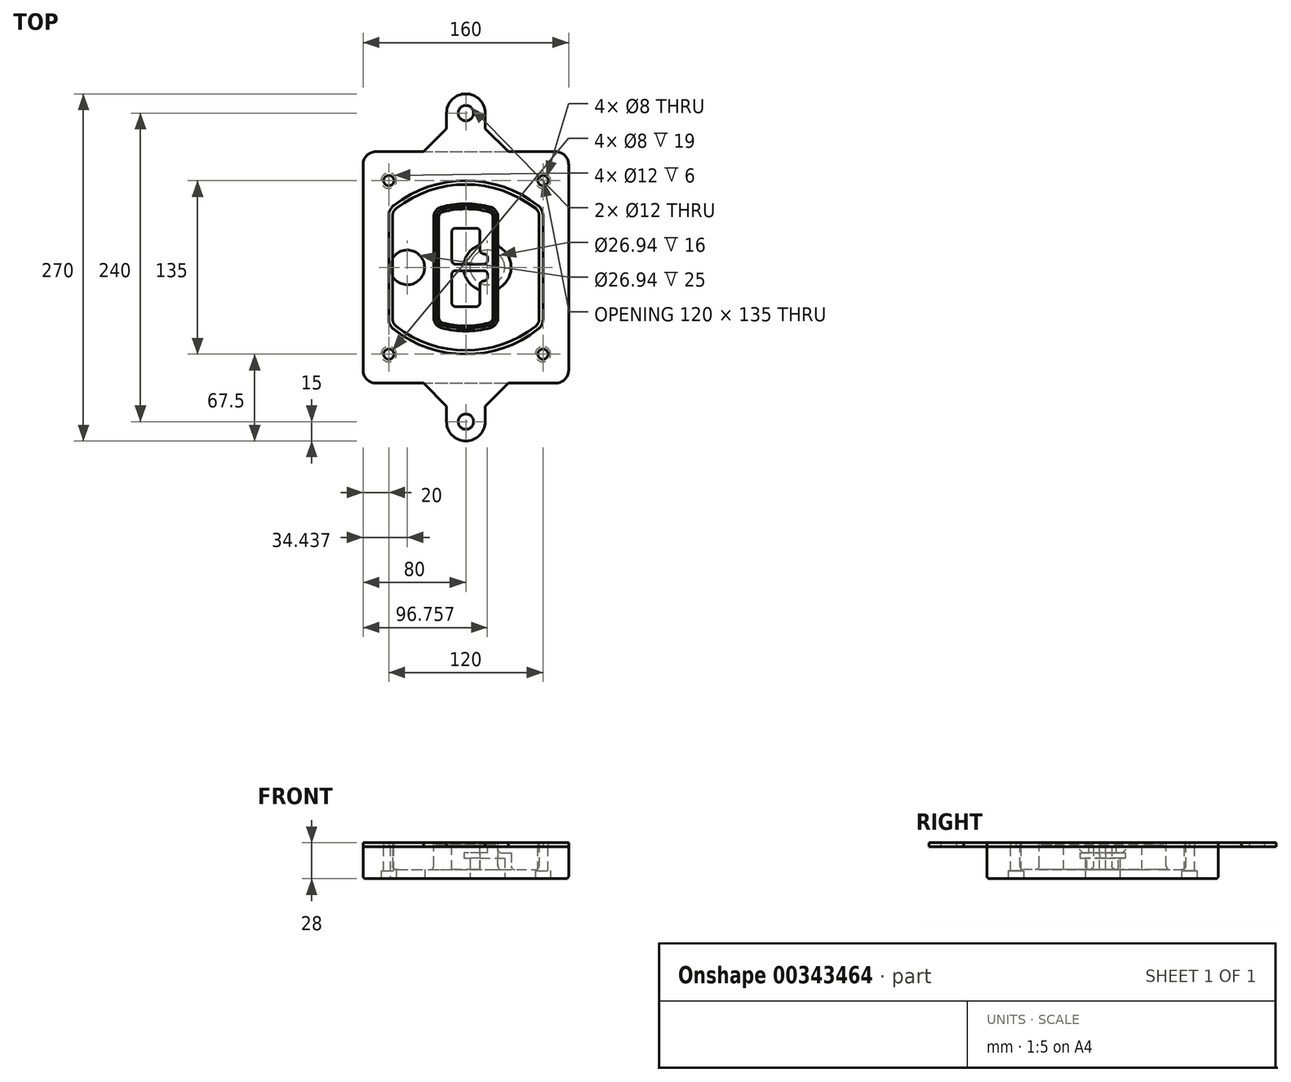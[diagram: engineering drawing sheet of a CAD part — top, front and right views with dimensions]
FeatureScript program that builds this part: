
annotation { "Feature Type Name" : "Feature", "Feature Type Description" : "" }
export const myFeature = defineFeature(function(context is Context, id is Id, definition is map)
    precondition{}
    {
        {
            var Q0;
            Q0=qCreatedBy(makeId("Top.planeOp"),FACE);
            var sketch = newSketch(context, id + "F0", { "sketchPlane" : qUnion([Q0])});
            skPoint(sketch, "E0.rect.middle", {"position": v(0, 0) * mm});
            skLineSegment(sketch, "E1.bottom", {"start": v(-70, -90) * mm, "end": v(70, -90) * mm});
            skLineSegment(sketch, "E1.top", {"start": v(-70, 90) * mm, "end": v(70, 90) * mm});
            skLineSegment(sketch, "E1.left", {"start": v(-80, -80) * mm, "end": v(-80, 80) * mm});
            skLineSegment(sketch, "E1.right", {"start": v(80, -80) * mm, "end": v(80, 80) * mm});
            skLineSegment(sketch, "E2", {"start": v(-80, 90) * mm, "end": v(80, -90) * mm, "construction": true});
            skLineSegment(sketch, "E3", {"start": v(80, 90) * mm, "end": v(-80, -90) * mm, "construction": true});
            skCircle(sketch, "E4", {"center": v(-60, 67.5) * mm, "radius": 4 * mm});
            skCircle(sketch, "E5", {"center": v(60, 67.5) * mm, "radius": 4 * mm});
            skCircle(sketch, "E6", {"center": v(60, -67.5) * mm, "radius": 4 * mm});
            skCircle(sketch, "E7", {"center": v(-60, -67.5) * mm, "radius": 4 * mm});
            skLineSegment(sketch, "E8", {"start": v(-60, 67.5) * mm, "end": v(60, 67.5) * mm, "construction": true});
            skLineSegment(sketch, "E9", {"start": v(60, 67.5) * mm, "end": v(60, -67.5) * mm, "construction": true});
            skLineSegment(sketch, "E10", {"start": v(60, -67.5) * mm, "end": v(-60, -67.5) * mm, "construction": true});
            skLineSegment(sketch, "E11", {"start": v(-60, -67.5) * mm, "end": v(-60, 67.5) * mm, "construction": true});
            skLineSegment(sketch, "E12", {"start": v(-60, 40.3) * mm, "end": v(-60, -40.3) * mm});
            skLineSegment(sketch, "E13", {"start": v(60, 40.3) * mm, "end": v(60, -40.3) * mm});
            skArc(sketch, "E14", {"start": v(56.15, 48.18) * mm, "mid": v(0, 67.5) * mm, "end": v(-56.15, 48.18) * mm});
            skArc(sketch, "E15", {"start": v(-56.15, -48.18) * mm, "mid": v(0, -67.5) * mm, "end": v(56.15, -48.18) * mm});
            skLineSegment(sketch, "E16", {"start": v(-60, 0) * mm, "end": v(60, 0) * mm, "construction": true});
            skPoint(sketch, "E17.visualSharp", {"position": v(-60, -45) * mm});
            skArc(sketch, "E17.filletArc", {"start": v(-60, -40.3) * mm, "mid": v(-58.99, -44.68) * mm, "end": v(-56.15, -48.18) * mm});
            skPoint(sketch, "E18.visualSharp", {"position": v(-60, 45) * mm});
            skArc(sketch, "E18.filletArc", {"start": v(-56.15, 48.18) * mm, "mid": v(-58.99, 44.68) * mm, "end": v(-60, 40.3) * mm});
            skPoint(sketch, "E19.visualSharp", {"position": v(60, 45) * mm});
            skArc(sketch, "E19.filletArc", {"start": v(60, 40.3) * mm, "mid": v(58.99, 44.68) * mm, "end": v(56.15, 48.18) * mm});
            skPoint(sketch, "E20.visualSharp", {"position": v(60, -45) * mm});
            skArc(sketch, "E20.filletArc", {"start": v(56.15, -48.18) * mm, "mid": v(58.99, -44.68) * mm, "end": v(60, -40.3) * mm});
            skPoint(sketch, "E21.visualSharp", {"position": v(-80, 90) * mm});
            skArc(sketch, "E21.filletArc", {"start": v(-70, 90) * mm, "mid": v(-77.07, 87.07) * mm, "end": v(-80, 80) * mm});
            skPoint(sketch, "E22.visualSharp", {"position": v(80, 90) * mm});
            skArc(sketch, "E22.filletArc", {"start": v(80, 80) * mm, "mid": v(77.07, 87.07) * mm, "end": v(70, 90) * mm});
            skPoint(sketch, "E23.visualSharp", {"position": v(80, -90) * mm});
            skArc(sketch, "E23.filletArc", {"start": v(70, -90) * mm, "mid": v(77.07, -87.07) * mm, "end": v(80, -80) * mm});
            skPoint(sketch, "E24.visualSharp", {"position": v(-80, -90) * mm});
            skArc(sketch, "E24.filletArc", {"start": v(-80, -80) * mm, "mid": v(-77.07, -87.07) * mm, "end": v(-70, -90) * mm});
            skArc(sketch, "E25.0", {"start": v(57, 40.3) * mm, "mid": v(56.3, 43.36) * mm, "end": v(54.3, 45.81) * mm});
            skLineSegment(sketch, "E25.1", {"start": v(57, 40.3) * mm, "end": v(57, -40.3) * mm});
            skArc(sketch, "E25.2", {"start": v(54.3, -45.81) * mm, "mid": v(56.3, -43.36) * mm, "end": v(57, -40.3) * mm});
            skArc(sketch, "E25.3", {"start": v(-54.3, -45.81) * mm, "mid": v(0, -64.5) * mm, "end": v(54.3, -45.81) * mm});
            skArc(sketch, "E25.4", {"start": v(-57, -40.3) * mm, "mid": v(-56.3, -43.36) * mm, "end": v(-54.3, -45.81) * mm});
            skArc(sketch, "E25.5", {"start": v(54.3, 45.81) * mm, "mid": v(0, 64.5) * mm, "end": v(-54.3, 45.81) * mm});
            skLineSegment(sketch, "E25.6", {"start": v(-57, 40.3) * mm, "end": v(-57, -40.3) * mm});
            skArc(sketch, "E25.7", {"start": v(-54.3, 45.81) * mm, "mid": v(-56.3, 43.36) * mm, "end": v(-57, 40.3) * mm});
            skArc(sketch, "E26.0", {"start": v(-58.62, 51.33) * mm, "mid": v(-62.58, 46.43) * mm, "end": v(-64, 40.3) * mm});
            skArc(sketch, "E26.1", {"start": v(58.62, 51.33) * mm, "mid": v(0, 71.5) * mm, "end": v(-58.62, 51.33) * mm});
            skArc(sketch, "E26.2", {"start": v(64, 40.3) * mm, "mid": v(62.58, 46.43) * mm, "end": v(58.62, 51.33) * mm});
            skLineSegment(sketch, "E26.3", {"start": v(64, 40.3) * mm, "end": v(64, -40.3) * mm});
            skArc(sketch, "E26.4", {"start": v(58.62, -51.33) * mm, "mid": v(62.58, -46.43) * mm, "end": v(64, -40.3) * mm});
            skLineSegment(sketch, "E26.5", {"start": v(-64, 40.3) * mm, "end": v(-64, -40.3) * mm});
            skArc(sketch, "E26.6", {"start": v(-58.62, -51.33) * mm, "mid": v(0, -71.5) * mm, "end": v(58.62, -51.33) * mm});
            skArc(sketch, "E26.7", {"start": v(-64, -40.3) * mm, "mid": v(-62.58, -46.43) * mm, "end": v(-58.62, -51.33) * mm});
            skSolve(sketch);
        }
        {
            var Q0;
            Q0=makeQuery(id+"F0.imprint","IMPRINT",FACE,{"disambiguationData":[TD([[makeQuery(id+"F0.imprint","IMPRINT",EDGE,{"derivedFrom":sQuery(id+"F0.wireOp",EDGE,"E1.bottom")}),1.0]])]});
            var Q1;
            Q1=makeQuery(id+"F0.imprint","IMPRINT",FACE,{"disambiguationData":[TD([[makeQuery(id+"F0.imprint","IMPRINT",EDGE,{"derivedFrom":sQuery(id+"F0.wireOp",EDGE,"E12")}),1.0]])]});
            var Q2;
            Q2=makeQuery(id+"F0.imprint","IMPRINT",FACE,{"disambiguationData":[TD([[makeQuery(id+"F0.imprint","IMPRINT",EDGE,{"derivedFrom":sQuery(id+"F0.wireOp",EDGE,"E25.0")}),1.0]])]});
            var Q3;
            Q3=makeQuery(id+"F0.imprint","IMPRINT",FACE,{"disambiguationData":[TD([[makeQuery(id+"F0.imprint","IMPRINT",EDGE,{"derivedFrom":sQuery(id+"F0.wireOp",EDGE,"E12")}),-1.0]])]});
            extrude(context, id + "F1", {"entities" : qUnion([Q0, Q1, Q2, Q3]), "oppositeDirection" : true, "depth" : 25 * mm});
        }
        {
            var Q0;
            Q0=makeQuery(id+"F0.imprint","IMPRINT",FACE,{"disambiguationData":[TD([[makeQuery(id+"F0.imprint","IMPRINT",EDGE,{"derivedFrom":sQuery(id+"F0.wireOp",EDGE,"E12")}),1.0]])]});
            extrude(context, id + "F2", {"entities" : qUnion([Q0]), "operationType" : NewBodyOperationType.ADD, "depth" : 3 * mm});
        }
        {
            var Q0;
            Q0=makeQuery(id+"F0.imprint","IMPRINT",FACE,{"disambiguationData":[TD([[makeQuery(id+"F0.imprint","IMPRINT",EDGE,{"derivedFrom":sQuery(id+"F0.wireOp",EDGE,"E25.0")}),1.0]])]});
            extrude(context, id + "F3", {"entities" : qUnion([Q0]), "operationType" : NewBodyOperationType.REMOVE, "oppositeDirection" : true, "depth" : 18 * mm});
        }
        {
            var Q0;
            Q0=makeQuery(id+"F2.opExtrude","CAP_FACE",FACE,{"disambiguationData":[OSD([sQuery(id+"F0.wireOp",EDGE,"E12"),sQuery(id+"F0.wireOp",EDGE,"E13"),sQuery(id+"F0.wireOp",EDGE,"E14"),sQuery(id+"F0.wireOp",EDGE,"E15"),sQuery(id+"F0.wireOp",EDGE,"E17.filletArc"),sQuery(id+"F0.wireOp",EDGE,"E18.filletArc"),sQuery(id+"F0.wireOp",EDGE,"E19.filletArc"),sQuery(id+"F0.wireOp",EDGE,"E20.filletArc"),sQuery(id+"F0.wireOp",EDGE,"E25.0"),sQuery(id+"F0.wireOp",EDGE,"E25.1"),sQuery(id+"F0.wireOp",EDGE,"E25.2"),sQuery(id+"F0.wireOp",EDGE,"E25.3"),sQuery(id+"F0.wireOp",EDGE,"E25.4"),sQuery(id+"F0.wireOp",EDGE,"E25.5"),sQuery(id+"F0.wireOp",EDGE,"E25.6"),sQuery(id+"F0.wireOp",EDGE,"E25.7")])],"isStart":false});
            var sketch = newSketch(context, id + "F4", { "sketchPlane" : qUnion([Q0])});
            skArc(sketch, "E27.0", {"start": v(-19.08, -46.97) * mm, "mid": v(0, -49.5) * mm, "end": v(19.08, -46.97) * mm});
            skArc(sketch, "E28.0", {"start": v(19.08, 46.97) * mm, "mid": v(0, 49.5) * mm, "end": v(-19.08, 46.97) * mm});
            skLineSegment(sketch, "E29", {"start": v(-25, 39.25) * mm, "end": v(-25, -39.25) * mm});
            skLineSegment(sketch, "E30", {"start": v(25, 39.25) * mm, "end": v(25, -39.25) * mm});
            skLineSegment(sketch, "E31", {"start": v(-25, 45.1) * mm, "end": v(25, 45.1) * mm, "construction": true});
            skLineSegment(sketch, "E32", {"start": v(-25, -45.1) * mm, "end": v(25, -45.1) * mm, "construction": true});
            skPoint(sketch, "E33.visualSharp", {"position": v(-25, 45.1) * mm});
            skArc(sketch, "E33.filletArc", {"start": v(-19.08, 46.97) * mm, "mid": v(-23.35, 44.11) * mm, "end": v(-25, 39.25) * mm});
            skPoint(sketch, "E34.visualSharp", {"position": v(25, 45.1) * mm});
            skArc(sketch, "E34.filletArc", {"start": v(25, 39.25) * mm, "mid": v(23.35, 44.11) * mm, "end": v(19.08, 46.97) * mm});
            skPoint(sketch, "E35.visualSharp", {"position": v(25, -45.1) * mm});
            skArc(sketch, "E35.filletArc", {"start": v(19.08, -46.97) * mm, "mid": v(23.35, -44.11) * mm, "end": v(25, -39.25) * mm});
            skPoint(sketch, "E36.visualSharp", {"position": v(-25, -45.1) * mm});
            skArc(sketch, "E36.filletArc", {"start": v(-25, -39.25) * mm, "mid": v(-23.35, -44.11) * mm, "end": v(-19.08, -46.97) * mm});
            skArc(sketch, "E37.0", {"start": v(54.3, 45.81) * mm, "mid": v(0, 64.5) * mm, "end": v(-54.3, 45.81) * mm});
            skArc(sketch, "E37.1", {"start": v(-54.3, 45.81) * mm, "mid": v(-56.3, 43.36) * mm, "end": v(-57, 40.3) * mm});
            skLineSegment(sketch, "E37.2", {"start": v(-57, 40.3) * mm, "end": v(-57, -40.3) * mm});
            skArc(sketch, "E37.3", {"start": v(-57, -40.3) * mm, "mid": v(-56.3, -43.36) * mm, "end": v(-54.3, -45.81) * mm});
            skArc(sketch, "E37.4", {"start": v(-54.3, -45.81) * mm, "mid": v(0, -64.5) * mm, "end": v(54.3, -45.81) * mm});
            skArc(sketch, "E37.5", {"start": v(54.3, -45.81) * mm, "mid": v(56.3, -43.36) * mm, "end": v(57, -40.3) * mm});
            skLineSegment(sketch, "E37.6", {"start": v(57, 40.3) * mm, "end": v(57, -40.3) * mm});
            skArc(sketch, "E37.7", {"start": v(57, 40.3) * mm, "mid": v(56.3, 43.36) * mm, "end": v(54.3, 45.81) * mm});
            skLineSegment(sketch, "E38.0", {"start": v(23, 39.25) * mm, "end": v(23, -39.25) * mm});
            skArc(sketch, "E38.1", {"start": v(18.56, -45.04) * mm, "mid": v(21.76, -42.9) * mm, "end": v(23, -39.25) * mm});
            skArc(sketch, "E38.2", {"start": v(-18.56, -45.04) * mm, "mid": v(0, -47.5) * mm, "end": v(18.56, -45.04) * mm});
            skArc(sketch, "E38.3", {"start": v(-23, -39.25) * mm, "mid": v(-21.76, -42.9) * mm, "end": v(-18.56, -45.04) * mm});
            skLineSegment(sketch, "E38.4", {"start": v(-23, 39.25) * mm, "end": v(-23, -39.25) * mm});
            skArc(sketch, "E38.5", {"start": v(23, 39.25) * mm, "mid": v(21.76, 42.9) * mm, "end": v(18.56, 45.04) * mm});
            skArc(sketch, "E38.6", {"start": v(-18.56, 45.04) * mm, "mid": v(-21.76, 42.9) * mm, "end": v(-23, 39.25) * mm});
            skArc(sketch, "E38.7", {"start": v(18.56, 45.04) * mm, "mid": v(0, 47.5) * mm, "end": v(-18.56, 45.04) * mm});
            skArc(sketch, "E39.0", {"start": v(21, 39.25) * mm, "mid": v(20.18, 41.68) * mm, "end": v(18.04, 43.1) * mm});
            skLineSegment(sketch, "E39.1", {"start": v(21, 39.25) * mm, "end": v(21, -39.25) * mm});
            skArc(sketch, "E39.2", {"start": v(18.04, -43.1) * mm, "mid": v(20.18, -41.68) * mm, "end": v(21, -39.25) * mm});
            skArc(sketch, "E39.3", {"start": v(-18.04, -43.1) * mm, "mid": v(0, -45.5) * mm, "end": v(18.04, -43.1) * mm});
            skArc(sketch, "E39.4", {"start": v(-21, -39.25) * mm, "mid": v(-20.18, -41.68) * mm, "end": v(-18.04, -43.1) * mm});
            skArc(sketch, "E39.5", {"start": v(18.04, 43.1) * mm, "mid": v(0, 45.5) * mm, "end": v(-18.04, 43.1) * mm});
            skLineSegment(sketch, "E39.6", {"start": v(-21, 39.25) * mm, "end": v(-21, -39.25) * mm});
            skArc(sketch, "E39.7", {"start": v(-18.04, 43.1) * mm, "mid": v(-20.18, 41.68) * mm, "end": v(-21, 39.25) * mm});
            skLineSegment(sketch, "E40", {"start": v(-25, 0) * mm, "end": v(25, 0) * mm, "construction": true});
            skLineSegment(sketch, "E41", {"start": v(-11, 5.5) * mm, "end": v(-11, 27.5) * mm});
            skLineSegment(sketch, "E42", {"start": v(-8, 30.5) * mm, "end": v(8, 30.5) * mm});
            skLineSegment(sketch, "E43", {"start": v(11, 27.5) * mm, "end": v(11, 13.5) * mm});
            skLineSegment(sketch, "E44", {"start": v(14, 10.5) * mm, "end": v(14, 10.5) * mm});
            skLineSegment(sketch, "E45", {"start": v(17, 7.5) * mm, "end": v(17, 5.5) * mm});
            skLineSegment(sketch, "E46", {"start": v(14, 2.5) * mm, "end": v(-8, 2.5) * mm});
            skPoint(sketch, "E47.visualSharp", {"position": v(-11, 30.5) * mm});
            skArc(sketch, "E47.filletArc", {"start": v(-8, 30.5) * mm, "mid": v(-10.12, 29.62) * mm, "end": v(-11, 27.5) * mm});
            skPoint(sketch, "E48.visualSharp", {"position": v(11, 30.5) * mm});
            skArc(sketch, "E48.filletArc", {"start": v(11, 27.5) * mm, "mid": v(10.12, 29.62) * mm, "end": v(8, 30.5) * mm});
            skPoint(sketch, "E49.visualSharp", {"position": v(11, 10.5) * mm});
            skArc(sketch, "E49.filletArc", {"start": v(11, 13.5) * mm, "mid": v(11.88, 11.38) * mm, "end": v(14, 10.5) * mm});
            skPoint(sketch, "E50.visualSharp", {"position": v(17, 10.5) * mm});
            skArc(sketch, "E50.filletArc", {"start": v(17, 7.5) * mm, "mid": v(16.12, 9.62) * mm, "end": v(14, 10.5) * mm});
            skPoint(sketch, "E51.visualSharp", {"position": v(17, 2.5) * mm});
            skArc(sketch, "E51.filletArc", {"start": v(14, 2.5) * mm, "mid": v(16.12, 3.38) * mm, "end": v(17, 5.5) * mm});
            skPoint(sketch, "E52.visualSharp", {"position": v(-11, 2.5) * mm});
            skArc(sketch, "E52.filletArc", {"start": v(-11, 5.5) * mm, "mid": v(-10.12, 3.38) * mm, "end": v(-8, 2.5) * mm});
            skLineSegment(sketch, "E53.0.MirrorCS", {"start": v(14, -2.5) * mm, "end": v(-8, -2.5) * mm});
            skArc(sketch, "E54.0.MirrorCS", {"start": v(-11, -5.5) * mm, "mid": v(-10.12, -3.38) * mm, "end": v(-8, -2.5) * mm});
            skLineSegment(sketch, "E55.0.MirrorCS", {"start": v(-11, -5.5) * mm, "end": v(-11, -27.5) * mm});
            skArc(sketch, "E56.0.MirrorCS", {"start": v(-8, -30.5) * mm, "mid": v(-10.12, -29.62) * mm, "end": v(-11, -27.5) * mm});
            skLineSegment(sketch, "E57.0.MirrorCS", {"start": v(-8, -30.5) * mm, "end": v(8, -30.5) * mm});
            skArc(sketch, "E58.0.MirrorCS", {"start": v(11, -27.5) * mm, "mid": v(10.12, -29.62) * mm, "end": v(8, -30.5) * mm});
            skLineSegment(sketch, "E59.0.MirrorCS", {"start": v(11, -27.5) * mm, "end": v(11, -13.5) * mm});
            skArc(sketch, "E60.0.MirrorCS", {"start": v(11, -13.5) * mm, "mid": v(11.88, -11.38) * mm, "end": v(14, -10.5) * mm});
            skArc(sketch, "E61.0.MirrorCS", {"start": v(17, -7.5) * mm, "mid": v(16.12, -9.62) * mm, "end": v(14, -10.5) * mm});
            skLineSegment(sketch, "E62.0.MirrorCS", {"start": v(17, -7.5) * mm, "end": v(17, -5.5) * mm});
            skArc(sketch, "E63.0.MirrorCS", {"start": v(14, -2.5) * mm, "mid": v(16.12, -3.38) * mm, "end": v(17, -5.5) * mm});
            skSolve(sketch);
        }
        {
            var Q0;
            Q0=makeQuery(id+"F4.imprint","IMPRINT",FACE,{"disambiguationData":[TD([[makeQuery(id+"F4.imprint","IMPRINT",EDGE,{"derivedFrom":sQuery(id+"F4.wireOp",EDGE,"E27.0")}),1.0]])]});
            var Q1;
            Q1=makeQuery(id+"F4.imprint","IMPRINT",FACE,{"disambiguationData":[TD([[makeQuery(id+"F4.imprint","IMPRINT",EDGE,{"derivedFrom":sQuery(id+"F4.wireOp",EDGE,"E38.0")}),-1.0]])]});
            var Q2;
            Q2=makeQuery(id+"F4.imprint","IMPRINT",FACE,{"disambiguationData":[TD([[makeQuery(id+"F4.imprint","IMPRINT",EDGE,{"derivedFrom":sQuery(id+"F4.wireOp",EDGE,"E39.0")}),1.0]])]});
            extrude(context, id + "F5", {"entities" : qUnion([Q0, Q1, Q2]), "operationType" : NewBodyOperationType.ADD, "endBound" : BoundingType.UP_TO_NEXT, "oppositeDirection" : true, "depth" : 25 * mm});
        }
        {
            var Q0;
            Q0=makeQuery(id+"F4.imprint","IMPRINT",FACE,{"disambiguationData":[TD([[makeQuery(id+"F4.imprint","IMPRINT",EDGE,{"derivedFrom":sQuery(id+"F4.wireOp",EDGE,"E38.0")}),-1.0]])]});
            extrude(context, id + "F6", {"entities" : qUnion([Q0]), "operationType" : NewBodyOperationType.REMOVE, "oppositeDirection" : true, "depth" : 2 * mm});
        }
        {
            var Q0;
            Q0=makeQuery(id+"F1.opExtrude","CAP_FACE",FACE,{"disambiguationData":[OSD([sQuery(id+"F0.wireOp",EDGE,"E1.bottom"),sQuery(id+"F0.wireOp",EDGE,"E1.top"),sQuery(id+"F0.wireOp",EDGE,"E1.left"),sQuery(id+"F0.wireOp",EDGE,"E1.right"),sQuery(id+"F0.wireOp",EDGE,"E4"),sQuery(id+"F0.wireOp",EDGE,"E5"),sQuery(id+"F0.wireOp",EDGE,"E6"),sQuery(id+"F0.wireOp",EDGE,"E7"),sQuery(id+"F0.wireOp",EDGE,"E21.filletArc"),sQuery(id+"F0.wireOp",EDGE,"E22.filletArc"),sQuery(id+"F0.wireOp",EDGE,"E23.filletArc"),sQuery(id+"F0.wireOp",EDGE,"E24.filletArc")])],"isStart":false});
            var sketch = newSketch(context, id + "F7", { "sketchPlane" : qUnion([Q0])});
            skCircle(sketch, "E64", {"center": v(16.76, 0) * mm, "radius": 13.47 * mm});
            skCircle(sketch, "E65", {"center": v(-45.56, 0) * mm, "radius": 13.47 * mm});
            skLineSegment(sketch, "E66", {"start": v(80, 0) * mm, "end": v(-80, 0) * mm});
            skCircle(sketch, "E67", {"center": v(16.76, 0) * mm, "radius": 18.47 * mm});
            skCircle(sketch, "E68", {"center": v(60, -67.5) * mm, "radius": 6 * mm});
            skCircle(sketch, "E69", {"center": v(-60, -67.5) * mm, "radius": 6 * mm});
            skCircle(sketch, "E70", {"center": v(-60, 67.5) * mm, "radius": 6 * mm});
            skCircle(sketch, "E71", {"center": v(60, 67.5) * mm, "radius": 6 * mm});
            skSolve(sketch);
        }
        {
            var Q0;
            {var subQ1=sQuery(id+"F7.wireOp",EDGE,"E66");var subQ4=sQuery(id+"F7.wireOp",EDGE,"E64");var subQ6=makeQuery(id+"F7.imprint","INTERSECT",VERTEX,{"disambiguationData":[OD(0.0)],"derivedFrom":[subQ4,subQ1]});Q0=makeQuery(id+"F7.imprint","IMPRINT",FACE,{"disambiguationData":[TD([[makeQuery(id+"F7.imprint","IMPRINT",EDGE,{"disambiguationData":[TD([[subQ6,-1.0]])],"derivedFrom":subQ4}),-1.0]])]});}
            var Q1;
            {var subQ0=sQuery(id+"F7.wireOp",EDGE,"E66");var subQ1=sQuery(id+"F7.wireOp",EDGE,"E64");var subQ3=makeQuery(id+"F7.imprint","INTERSECT",VERTEX,{"disambiguationData":[OD(0.0)],"derivedFrom":[subQ1,subQ0]});Q1=makeQuery(id+"F7.imprint","IMPRINT",FACE,{"disambiguationData":[TD([[makeQuery(id+"F7.imprint","IMPRINT",EDGE,{"disambiguationData":[TD([[subQ3,-1.0]])],"derivedFrom":subQ1}),1.0]])]});}
            var Q2;
            {var subQ0=sQuery(id+"F7.wireOp",EDGE,"E66");var subQ1=sQuery(id+"F7.wireOp",EDGE,"E64");var subQ3=makeQuery(id+"F7.imprint","INTERSECT",VERTEX,{"disambiguationData":[OD(0.0)],"derivedFrom":[subQ1,subQ0]});Q2=makeQuery(id+"F7.imprint","IMPRINT",FACE,{"disambiguationData":[TD([[makeQuery(id+"F7.imprint","IMPRINT",EDGE,{"disambiguationData":[TD([[subQ3,1.0]])],"derivedFrom":subQ1}),1.0]])]});}
            var Q3;
            {var subQ1=sQuery(id+"F7.wireOp",EDGE,"E66");var subQ4=sQuery(id+"F7.wireOp",EDGE,"E64");var subQ6=makeQuery(id+"F7.imprint","INTERSECT",VERTEX,{"disambiguationData":[OD(0.0)],"derivedFrom":[subQ4,subQ1]});Q3=makeQuery(id+"F7.imprint","IMPRINT",FACE,{"disambiguationData":[TD([[makeQuery(id+"F7.imprint","IMPRINT",EDGE,{"disambiguationData":[TD([[subQ6,1.0]])],"derivedFrom":subQ4}),-1.0]])]});}
            extrude(context, id + "F8", {"entities" : qUnion([Q0, Q1, Q2, Q3]), "operationType" : NewBodyOperationType.ADD, "oppositeDirection" : true, "depth" : 20 * mm});
        }
        {
            var Q0;
            {var subQ0=sQuery(id+"F7.wireOp",EDGE,"E66");var subQ1=sQuery(id+"F7.wireOp",EDGE,"E64");var subQ3=makeQuery(id+"F7.imprint","INTERSECT",VERTEX,{"disambiguationData":[OD(0.0)],"derivedFrom":[subQ1,subQ0]});Q0=makeQuery(id+"F7.imprint","IMPRINT",FACE,{"disambiguationData":[TD([[makeQuery(id+"F7.imprint","IMPRINT",EDGE,{"disambiguationData":[TD([[subQ3,-1.0]])],"derivedFrom":subQ1}),1.0]])]});}
            var Q1;
            {var subQ0=sQuery(id+"F7.wireOp",EDGE,"E66");var subQ1=sQuery(id+"F7.wireOp",EDGE,"E64");var subQ3=makeQuery(id+"F7.imprint","INTERSECT",VERTEX,{"disambiguationData":[OD(0.0)],"derivedFrom":[subQ1,subQ0]});Q1=makeQuery(id+"F7.imprint","IMPRINT",FACE,{"disambiguationData":[TD([[makeQuery(id+"F7.imprint","IMPRINT",EDGE,{"disambiguationData":[TD([[subQ3,1.0]])],"derivedFrom":subQ1}),1.0]])]});}
            extrude(context, id + "F9", {"entities" : qUnion([Q0, Q1]), "operationType" : NewBodyOperationType.REMOVE, "oppositeDirection" : true, "depth" : 16 * mm});
        }
        {
            var Q0;
            {var subQ0=sQuery(id+"F7.wireOp",EDGE,"E66");var subQ1=sQuery(id+"F7.wireOp",EDGE,"E65");var subQ3=makeQuery(id+"F7.imprint","INTERSECT",VERTEX,{"disambiguationData":[OD(0.0)],"derivedFrom":[subQ1,subQ0]});Q0=makeQuery(id+"F7.imprint","IMPRINT",FACE,{"disambiguationData":[TD([[makeQuery(id+"F7.imprint","IMPRINT",EDGE,{"disambiguationData":[TD([[subQ3,-1.0]])],"derivedFrom":subQ1}),1.0]])]});}
            var Q1;
            {var subQ0=sQuery(id+"F7.wireOp",EDGE,"E66");var subQ1=sQuery(id+"F7.wireOp",EDGE,"E65");var subQ3=makeQuery(id+"F7.imprint","INTERSECT",VERTEX,{"disambiguationData":[OD(0.0)],"derivedFrom":[subQ1,subQ0]});Q1=makeQuery(id+"F7.imprint","IMPRINT",FACE,{"disambiguationData":[TD([[makeQuery(id+"F7.imprint","IMPRINT",EDGE,{"disambiguationData":[TD([[subQ3,1.0]])],"derivedFrom":subQ1}),1.0]])]});}
            extrude(context, id + "F10", {"entities" : qUnion([Q0, Q1]), "operationType" : NewBodyOperationType.REMOVE, "oppositeDirection" : true, "depth" : 25 * mm});
        }
        {
            var Q0;
            Q0=makeQuery(id+"F7.imprint","IMPRINT",FACE,{"disambiguationData":[TD([[makeQuery(id+"F7.imprint","IMPRINT",EDGE,{"derivedFrom":sQuery(id+"F7.wireOp",EDGE,"E68")}),1.0]])]});
            var Q1;
            Q1=makeQuery(id+"F7.imprint","IMPRINT",FACE,{"disambiguationData":[TD([[makeQuery(id+"F7.imprint","IMPRINT",EDGE,{"derivedFrom":makeQuery(id+"F1.opExtrude","CAP_EDGE",EDGE,{"disambiguationData":[OSD([sQuery(id+"F0.wireOp",EDGE,"E5")])],"isStart":false})}),-1.0]])]});
            var Q2;
            Q2=makeQuery(id+"F7.imprint","IMPRINT",FACE,{"disambiguationData":[TD([[makeQuery(id+"F7.imprint","IMPRINT",EDGE,{"derivedFrom":sQuery(id+"F7.wireOp",EDGE,"E69")}),1.0]])]});
            var Q3;
            Q3=makeQuery(id+"F7.imprint","IMPRINT",FACE,{"disambiguationData":[TD([[makeQuery(id+"F7.imprint","IMPRINT",EDGE,{"derivedFrom":makeQuery(id+"F1.opExtrude","CAP_EDGE",EDGE,{"disambiguationData":[OSD([sQuery(id+"F0.wireOp",EDGE,"E4")])],"isStart":false})}),-1.0]])]});
            var Q4;
            Q4=makeQuery(id+"F7.imprint","IMPRINT",FACE,{"disambiguationData":[TD([[makeQuery(id+"F7.imprint","IMPRINT",EDGE,{"derivedFrom":sQuery(id+"F7.wireOp",EDGE,"E70")}),1.0]])]});
            var Q5;
            Q5=makeQuery(id+"F7.imprint","IMPRINT",FACE,{"disambiguationData":[TD([[makeQuery(id+"F7.imprint","IMPRINT",EDGE,{"derivedFrom":makeQuery(id+"F1.opExtrude","CAP_EDGE",EDGE,{"disambiguationData":[OSD([sQuery(id+"F0.wireOp",EDGE,"E7")])],"isStart":false})}),-1.0]])]});
            var Q6;
            Q6=makeQuery(id+"F7.imprint","IMPRINT",FACE,{"disambiguationData":[TD([[makeQuery(id+"F7.imprint","IMPRINT",EDGE,{"derivedFrom":sQuery(id+"F7.wireOp",EDGE,"E71")}),1.0]])]});
            var Q7;
            Q7=makeQuery(id+"F7.imprint","IMPRINT",FACE,{"disambiguationData":[TD([[makeQuery(id+"F7.imprint","IMPRINT",EDGE,{"derivedFrom":makeQuery(id+"F1.opExtrude","CAP_EDGE",EDGE,{"disambiguationData":[OSD([sQuery(id+"F0.wireOp",EDGE,"E6")])],"isStart":false})}),-1.0]])]});
            extrude(context, id + "F11", {"entities" : qUnion([Q0, Q1, Q2, Q3, Q4, Q5, Q6, Q7]), "operationType" : NewBodyOperationType.REMOVE, "oppositeDirection" : true, "depth" : 6 * mm});
        }
        {
            var Q0;
            Q0=makeQuery(id+"F9.boolean.opBoolean","COPY",FACE,{"derivedFrom":makeQuery(id+"F9.opExtrude","CAP_FACE",FACE,{"disambiguationData":[OSD([sQuery(id+"F7.wireOp",EDGE,"E64")])],"isStart":false})});
            var sketch = newSketch(context, id + "F12", { "sketchPlane" : qUnion([Q0])});
            skArc(sketch, "E72.0", {"start": v(11, 17.55) * mm, "mid": v(2.57, 11.82) * mm, "end": v(-1.54, 2.5) * mm});
            skArc(sketch, "E72.1", {"start": v(-1.54, -2.5) * mm, "mid": v(2.57, -11.82) * mm, "end": v(11, -17.55) * mm});
            skLineSegment(sketch, "E73", {"start": v(-1.54, -2.5) * mm, "end": v(14, -2.5) * mm});
            skLineSegment(sketch, "E74.0", {"start": v(14, 2.5) * mm, "end": v(-1.54, 2.5) * mm});
            skArc(sketch, "E74.1", {"start": v(14, 2.5) * mm, "mid": v(16.12, 3.38) * mm, "end": v(17, 5.5) * mm});
            skLineSegment(sketch, "E74.2", {"start": v(17, 7.5) * mm, "end": v(17, 5.5) * mm});
            skArc(sketch, "E74.3", {"start": v(17, 7.5) * mm, "mid": v(16.12, 9.62) * mm, "end": v(14, 10.5) * mm});
            skArc(sketch, "E74.4", {"start": v(11, 13.5) * mm, "mid": v(11.88, 11.38) * mm, "end": v(14, 10.5) * mm});
            skLineSegment(sketch, "E74.5", {"start": v(11, 17.55) * mm, "end": v(11, 13.5) * mm});
            skLineSegment(sketch, "E74.7", {"start": v(14, -2.5) * mm, "end": v(-1.54, -2.5) * mm});
            skArc(sketch, "E74.8", {"start": v(14, -2.5) * mm, "mid": v(16.12, -3.38) * mm, "end": v(17, -5.5) * mm});
            skLineSegment(sketch, "E74.9", {"start": v(17, -7.5) * mm, "end": v(17, -5.5) * mm});
            skArc(sketch, "E74.10", {"start": v(17, -7.5) * mm, "mid": v(16.12, -9.62) * mm, "end": v(14, -10.5) * mm});
            skArc(sketch, "E74.11", {"start": v(11, -13.5) * mm, "mid": v(11.88, -11.38) * mm, "end": v(14, -10.5) * mm});
            skLineSegment(sketch, "E74.12", {"start": v(11, -17.55) * mm, "end": v(11, -13.5) * mm});
            skPoint(sketch, "E75.orphan", {"position": v(11, -27.5) * mm});
            skPoint(sketch, "E76.orphan", {"position": v(-8, -2.5) * mm});
            skPoint(sketch, "E77.orphan", {"position": v(-8, 2.5) * mm});
            skPoint(sketch, "E78.orphan", {"position": v(11, 27.5) * mm});
            skSolve(sketch);
        }
        {
            var Q0;
            {var subQ7=sQuery(id+"F12.wireOp",EDGE,"E72.0");var subQ14=sQuery(id+"F12.wireOp",EDGE,"E72.1");var subQ16=sQuery(id+"F12.wireOp",EDGE,"E74.1");var subQ18=sQuery(id+"F12.wireOp",EDGE,"E74.8");Q0=qUnion([makeQuery(id+"F12.imprint","IMPRINT",FACE,{"disambiguationData":[TD([[makeQuery(id+"F12.imprint","IMPRINT",EDGE,{"derivedFrom":subQ7}),1.0]])]}),makeQuery(id+"F12.imprint","IMPRINT",FACE,{"disambiguationData":[TD([[makeQuery(id+"F12.imprint","IMPRINT",EDGE,{"derivedFrom":subQ14}),1.0]])]}),makeQuery(id+"F12.imprint","IMPRINT",FACE,{"disambiguationData":[TD([[makeQuery(id+"F12.imprint","IMPRINT",EDGE,{"derivedFrom":subQ16}),1.0]])]}),makeQuery(id+"F12.imprint","IMPRINT",FACE,{"disambiguationData":[TD([[makeQuery(id+"F12.imprint","IMPRINT",EDGE,{"derivedFrom":subQ18}),-1.0]])]})]);}
            var Q1;
            Q1=makeQuery(id+"F5.boolean.opBoolean","SPLIT",FACE,{"disambiguationData":[TD([makeQuery(id+"F5.opExtrude","SWEPT_FACE",FACE,{"disambiguationData":[OSD([sQuery(id+"F4.wireOp",EDGE,"E41")])]})])],"derivedFrom":makeQuery(id+"F3.boolean.opBoolean","COPY",FACE,{"derivedFrom":makeQuery(id+"F3.opExtrude","CAP_FACE",FACE,{"disambiguationData":[OSD([sQuery(id+"F0.wireOp",EDGE,"E25.0"),sQuery(id+"F0.wireOp",EDGE,"E25.1"),sQuery(id+"F0.wireOp",EDGE,"E25.2"),sQuery(id+"F0.wireOp",EDGE,"E25.3"),sQuery(id+"F0.wireOp",EDGE,"E25.4"),sQuery(id+"F0.wireOp",EDGE,"E25.5"),sQuery(id+"F0.wireOp",EDGE,"E25.6"),sQuery(id+"F0.wireOp",EDGE,"E25.7")])],"isStart":false})})});
            extrude(context, id + "F13", {"entities" : qUnion([Q0]), "operationType" : NewBodyOperationType.REMOVE, "endBound" : BoundingType.UP_TO_SURFACE, "endBoundEntityFace" : qUnion([Q1]), "depth" : 25 * mm});
        }
        {
            var Q0;
            Q0=makeQuery(id+"F3.boolean.opBoolean","COPY",EDGE,{"derivedFrom":makeQuery(id+"F3.opExtrude","CAP_EDGE",EDGE,{"disambiguationData":[OSD([sQuery(id+"F0.wireOp",EDGE,"E25.6")])],"isStart":false})});
            var Q1;
            Q1=makeQuery(id+"F8.boolean.opBoolean","INTERSECT",EDGE,{"derivedFrom":[makeQuery(id+"F5.opExtrude","SWEPT_FACE",FACE,{"disambiguationData":[OSD([sQuery(id+"F4.wireOp",EDGE,"E30")])]}),makeQuery(id+"F8.opExtrude","CAP_FACE",FACE,{"disambiguationData":[OSD([sQuery(id+"F7.wireOp",EDGE,"E67")])],"isStart":false})]});
            var Q2;
            Q2=makeQuery(id+"F8.boolean.opBoolean","INTERSECT",EDGE,{"disambiguationData":[OD(1.0)],"derivedFrom":[makeQuery(id+"F5.opExtrude","SWEPT_FACE",FACE,{"disambiguationData":[OSD([sQuery(id+"F4.wireOp",EDGE,"E30")])]}),makeQuery(id+"F8.opExtrude","SWEPT_FACE",FACE,{"disambiguationData":[OSD([sQuery(id+"F7.wireOp",EDGE,"E67")])]})]});
            var Q3;
            {var subQ0=sQuery(id+"F4.wireOp",EDGE,"E30");Q3=makeQuery(id+"F8.boolean.opBoolean","SPLIT",EDGE,{"disambiguationData":[TD([makeQuery(id+"F5.opExtrude","SWEPT_FACE",FACE,{"disambiguationData":[OSD([sQuery(id+"F4.wireOp",EDGE,"E35.filletArc")])]})])],"derivedFrom":makeQuery(id+"F5.opExtrude","CAP_EDGE",EDGE,{"disambiguationData":[OSD([subQ0])],"isStart":false})});}
            var Q4;
            {var subQ0=sQuery(id+"F0.wireOp",EDGE,"E25.7");var subQ1=sQuery(id+"F0.wireOp",EDGE,"E25.1");var subQ2=sQuery(id+"F0.wireOp",EDGE,"E25.6");var subQ3=sQuery(id+"F0.wireOp",EDGE,"E25.5");var subQ4=sQuery(id+"F0.wireOp",EDGE,"E25.4");var subQ5=sQuery(id+"F0.wireOp",EDGE,"E25.0");var subQ6=sQuery(id+"F0.wireOp",EDGE,"E25.2");var subQ7=sQuery(id+"F0.wireOp",EDGE,"E25.3");Q4=makeQuery(id+"F8.boolean.opBoolean","INTERSECT",EDGE,{"derivedFrom":[makeQuery(id+"F5.boolean.opBoolean","SPLIT",FACE,{"disambiguationData":[TD([makeQuery(id+"F2.opExtrude","SWEPT_FACE",FACE,{"disambiguationData":[OSD([subQ5])]})])],"derivedFrom":makeQuery(id+"F3.boolean.opBoolean","COPY",FACE,{"derivedFrom":makeQuery(id+"F3.opExtrude","CAP_FACE",FACE,{"disambiguationData":[OSD([subQ5,subQ1,subQ6,subQ7,subQ4,subQ3,subQ2,subQ0])],"isStart":false})})}),makeQuery(id+"F8.opExtrude","SWEPT_FACE",FACE,{"disambiguationData":[OSD([sQuery(id+"F7.wireOp",EDGE,"E67")])]})]});}
            var Q5;
            Q5=makeQuery(id+"F8.boolean.opBoolean","INTERSECT",EDGE,{"disambiguationData":[OD(0.0)],"derivedFrom":[makeQuery(id+"F5.opExtrude","SWEPT_FACE",FACE,{"disambiguationData":[OSD([sQuery(id+"F4.wireOp",EDGE,"E30")])]}),makeQuery(id+"F8.opExtrude","SWEPT_FACE",FACE,{"disambiguationData":[OSD([sQuery(id+"F7.wireOp",EDGE,"E67")])]})]});
            fillet(context, id + "F14", {"entities" : qUnion([Q0, Q1, Q2, Q3, Q4, Q5]), "radius" : 3 * mm, "tangentPropagation" : true, "allowEdgeOverflow" : false});
        }
        {
            var Q0;
            Q0=makeQuery(id+"F1.opExtrude","CAP_EDGE",EDGE,{"disambiguationData":[OSD([sQuery(id+"F0.wireOp",EDGE,"E1.bottom")])],"isStart":false});
            fillet(context, id + "F15", {"entities" : qUnion([Q0]), "radius" : 2 * mm, "tangentPropagation" : true, "allowEdgeOverflow" : false});
        }
        {
            var Q0;
            {var subQ0=sQuery(id+"F0.wireOp",EDGE,"E21.filletArc");var subQ1=sQuery(id+"F0.wireOp",EDGE,"E7");var subQ2=sQuery(id+"F0.wireOp",EDGE,"E6");var subQ3=sQuery(id+"F0.wireOp",EDGE,"E5");var subQ4=sQuery(id+"F0.wireOp",EDGE,"E4");var subQ5=sQuery(id+"F0.wireOp",EDGE,"E22.filletArc");var subQ6=sQuery(id+"F0.wireOp",EDGE,"E1.bottom");var subQ7=sQuery(id+"F0.wireOp",EDGE,"E1.right");var subQ8=sQuery(id+"F0.wireOp",EDGE,"E1.top");var subQ9=sQuery(id+"F0.wireOp",EDGE,"E1.left");var subQ10=sQuery(id+"F0.wireOp",EDGE,"E23.filletArc");var subQ11=sQuery(id+"F0.wireOp",EDGE,"E24.filletArc");Q0=makeQuery(id+"F2.boolean.opBoolean","SPLIT",FACE,{"disambiguationData":[TD([makeQuery(id+"F1.opExtrude","SWEPT_FACE",FACE,{"disambiguationData":[OSD([subQ6])]})])],"derivedFrom":makeQuery(id+"F1.opExtrude","CAP_FACE",FACE,{"disambiguationData":[OSD([subQ6,subQ8,subQ9,subQ7,subQ4,subQ3,subQ2,subQ1,subQ0,subQ5,subQ10,subQ11])],"isStart":true})});}
            var sketch = newSketch(context, id + "F16", { "sketchPlane" : qUnion([Q0])});
            skLineSegment(sketch, "E79.0", {"start": v(-70, 90) * mm, "end": v(70, 90) * mm});
            skArc(sketch, "E79.1", {"start": v(-70, 90) * mm, "mid": v(-77.07, 87.07) * mm, "end": v(-80, 80) * mm});
            skLineSegment(sketch, "E79.2", {"start": v(-80, -80) * mm, "end": v(-80, 80) * mm});
            skCircle(sketch, "E79.3", {"center": v(-60, 67.5) * mm, "radius": 4 * mm});
            skArc(sketch, "E79.4", {"start": v(-56.15, 48.18) * mm, "mid": v(-58.99, 44.68) * mm, "end": v(-60, 40.3) * mm});
            skArc(sketch, "E79.5", {"start": v(56.15, 48.18) * mm, "mid": v(0, 67.5) * mm, "end": v(-56.15, 48.18) * mm});
            skLineSegment(sketch, "E79.6", {"start": v(-60, 40.3) * mm, "end": v(-60, -40.3) * mm});
            skArc(sketch, "E79.7", {"start": v(60, 40.3) * mm, "mid": v(58.99, 44.68) * mm, "end": v(56.15, 48.18) * mm});
            skCircle(sketch, "E79.8", {"center": v(60, 67.5) * mm, "radius": 4 * mm});
            skLineSegment(sketch, "E79.9", {"start": v(80, -80) * mm, "end": v(80, 80) * mm});
            skArc(sketch, "E79.10", {"start": v(80, 80) * mm, "mid": v(77.07, 87.07) * mm, "end": v(70, 90) * mm});
            skLineSegment(sketch, "E79.11", {"start": v(60, 40.3) * mm, "end": v(60, -40.3) * mm});
            skArc(sketch, "E79.12", {"start": v(56.15, -48.18) * mm, "mid": v(58.99, -44.68) * mm, "end": v(60, -40.3) * mm});
            skArc(sketch, "E79.13", {"start": v(-56.15, -48.18) * mm, "mid": v(0, -67.5) * mm, "end": v(56.15, -48.18) * mm});
            skCircle(sketch, "E79.14", {"center": v(60, -67.5) * mm, "radius": 4 * mm});
            skArc(sketch, "E79.15", {"start": v(70, -90) * mm, "mid": v(77.07, -87.07) * mm, "end": v(80, -80) * mm});
            skLineSegment(sketch, "E79.16", {"start": v(-70, -90) * mm, "end": v(70, -90) * mm});
            skCircle(sketch, "E79.17", {"center": v(-60, -67.5) * mm, "radius": 4 * mm});
            skArc(sketch, "E79.18", {"start": v(-80, -80) * mm, "mid": v(-77.07, -87.07) * mm, "end": v(-70, -90) * mm});
            skArc(sketch, "E79.19", {"start": v(-60, -40.3) * mm, "mid": v(-58.99, -44.68) * mm, "end": v(-56.15, -48.18) * mm});
            skLineSegment(sketch, "E80", {"start": v(0, 90) * mm, "end": v(0, 120) * mm, "construction": true});
            skPoint(sketch, "E80.endSnap0", {"position": v(0, 90) * mm});
            skCircle(sketch, "E81", {"center": v(0, 120) * mm, "radius": 6 * mm});
            skArc(sketch, "E82", {"start": v(15, 120) * mm, "mid": v(0, 135) * mm, "end": v(-15, 120) * mm});
            skLineSegment(sketch, "E83", {"start": v(-15, 120) * mm, "end": v(-15, 108) * mm});
            skLineSegment(sketch, "E84", {"start": v(-15, 108) * mm, "end": v(-33, 90) * mm});
            skLineSegment(sketch, "E85", {"start": v(15, 120) * mm, "end": v(15, 108) * mm});
            skLineSegment(sketch, "E86", {"start": v(15, 108) * mm, "end": v(33, 90) * mm});
            skLineSegment(sketch, "E87", {"start": v(-80, 0) * mm, "end": v(80, 0) * mm, "construction": true});
            skLineSegment(sketch, "E88.MirrorCS", {"start": v(-15, -108) * mm, "end": v(-33, -90) * mm});
            skLineSegment(sketch, "E89.MirrorCS", {"start": v(-15, -120) * mm, "end": v(-15, -108) * mm});
            skArc(sketch, "E90.MirrorCS", {"start": v(15, -120) * mm, "mid": v(0, -135) * mm, "end": v(-15, -120) * mm});
            skLineSegment(sketch, "E91.MirrorCS", {"start": v(15, -120) * mm, "end": v(15, -108) * mm});
            skLineSegment(sketch, "E92.MirrorCS", {"start": v(15, -108) * mm, "end": v(33, -90) * mm});
            skCircle(sketch, "E93.MirrorC", {"center": v(0, -120) * mm, "radius": 6 * mm});
            skSolve(sketch);
        }
        {
            var Q0;
            Q0 = qSketchRegion(id + "F16", true);
            var Q1;
            Q1=makeQuery(id+"F2.opExtrude","CAP_FACE",FACE,{"disambiguationData":[OSD([sQuery(id+"F0.wireOp",EDGE,"E12"),sQuery(id+"F0.wireOp",EDGE,"E13"),sQuery(id+"F0.wireOp",EDGE,"E14"),sQuery(id+"F0.wireOp",EDGE,"E15"),sQuery(id+"F0.wireOp",EDGE,"E17.filletArc"),sQuery(id+"F0.wireOp",EDGE,"E18.filletArc"),sQuery(id+"F0.wireOp",EDGE,"E19.filletArc"),sQuery(id+"F0.wireOp",EDGE,"E20.filletArc"),sQuery(id+"F0.wireOp",EDGE,"E25.0"),sQuery(id+"F0.wireOp",EDGE,"E25.1"),sQuery(id+"F0.wireOp",EDGE,"E25.2"),sQuery(id+"F0.wireOp",EDGE,"E25.3"),sQuery(id+"F0.wireOp",EDGE,"E25.4"),sQuery(id+"F0.wireOp",EDGE,"E25.5"),sQuery(id+"F0.wireOp",EDGE,"E25.6"),sQuery(id+"F0.wireOp",EDGE,"E25.7")])],"isStart":false});
            extrude(context, id + "F17", {"entities" : qUnion([Q0]), "endBound" : BoundingType.UP_TO_SURFACE, "endBoundEntityFace" : qUnion([Q1]), "depth" : 25 * mm});
        }
    });
